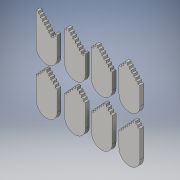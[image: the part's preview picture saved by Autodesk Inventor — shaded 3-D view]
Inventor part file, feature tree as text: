
AUTODESK INVENTOR PART (.ipt)
format: ipt  version: 2016 (Build 200138000, 138)  size: 399,360 bytes
history: native  units: in
note: dims shown in document units (in); Inventor stores cm internally (conversion verified against a paired STEP export)
features: extrude x1, sketch x1
ambient origin geometry x8: Origin, YZ Plane, XZ Plane, XY Plane, X Axis, Y Axis, Z Axis, Center Point
bodies: Solid1 (feature_tree)
feature tree (2):
  extrude  "Extrusion1"  Depth=0.1in
  sketch  "Sketch1"  dims[d2=0.1in d3=0.1in d4=0.1in d5=0.1in d6=0.1in d7=0.1in d8=0.1in d9=0.1in d20=0.1in d21=0.1in d22=0.1in d23=0.1in d24=0.1in d25=0.1in d26=0.1in d27=0.1in d28=0.1071in d29=0.1071in d30=0.1071in d31=0.1071in d32=0.1071in d33=0.1071in d34=0.1in d35=0.1in d36=0.1in d37=0.1in d38=0.1in d39=0.1in d40=0.1in d41=0.1in d42=0.1in d43=0.1in d44=0.1in d45=0.1in d46=0.1in d47=0.1in d48=0.1in d49=0.1in d50=0.1in d51=0.1in d52=0.1in d53=0.1in d54=0.18in d55=0.0in d59=0.1071in d60=0.1071in d61=0.1071in d62=0.1071in d63=0.1071in d64=0.1071in d65=0.1071in]
